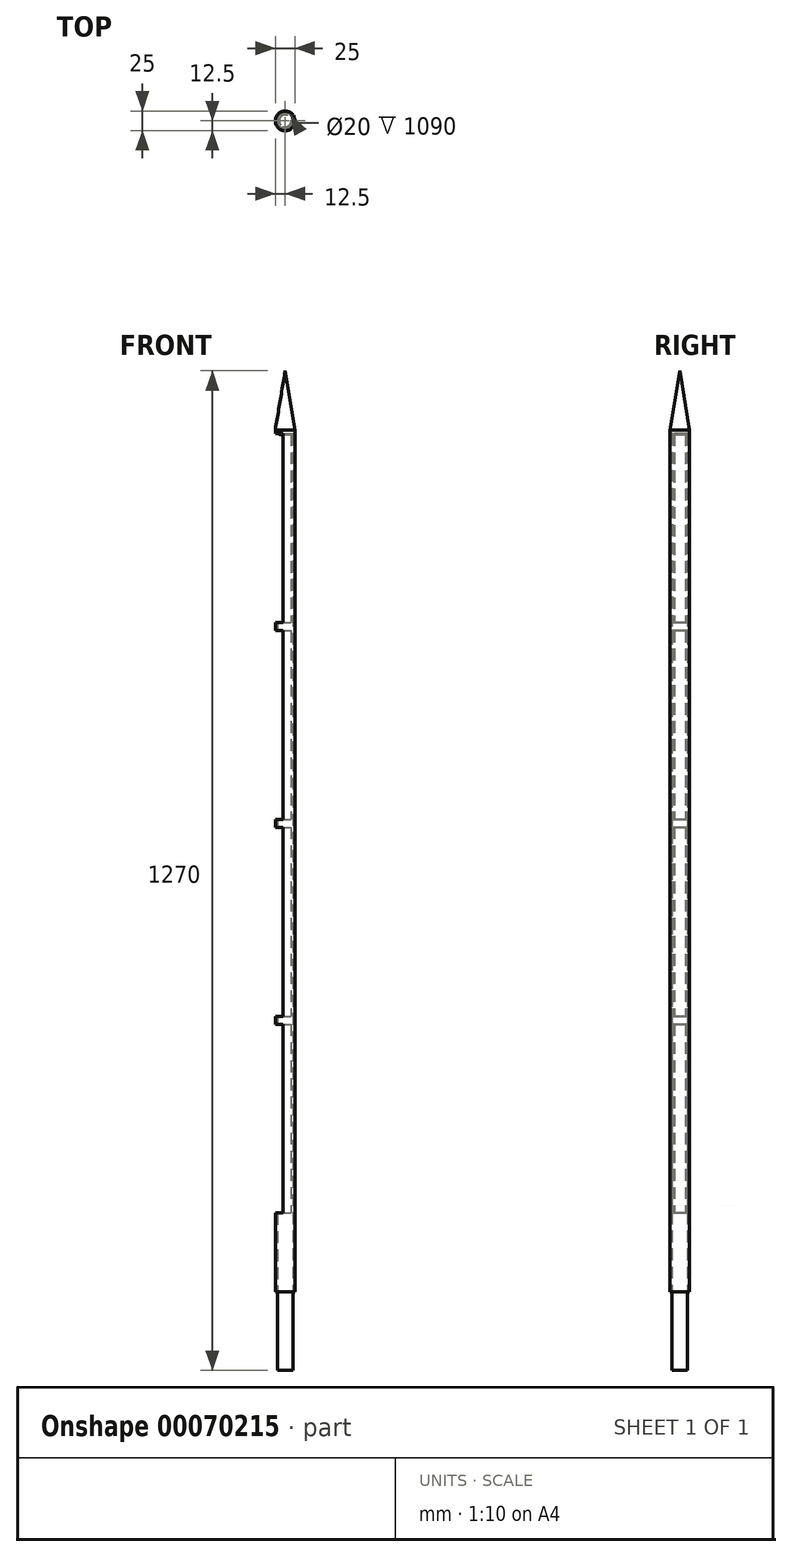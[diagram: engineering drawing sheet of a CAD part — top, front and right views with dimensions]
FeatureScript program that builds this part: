
annotation { "Feature Type Name" : "Feature", "Feature Type Description" : "" }
export const myFeature = defineFeature(function(context is Context, id is Id, definition is map)
    precondition{}
    {
        {
            var Q0;
            Q0=qCreatedBy(makeId("Top.planeOp"),FACE);
            var sketch = newSketch(context, id + "F0", { "sketchPlane" : qUnion([Q0])});
            skCircle(sketch, "E0", {"center": v(0, 0) * mm, "radius": 12.5 * mm});
            skCircle(sketch, "E1", {"center": v(0, 0) * mm, "radius": 9.9 * mm});
            skCircle(sketch, "E2", {"center": v(0, 0) * mm, "radius": 7.5 * mm});
            skCircle(sketch, "E3", {"center": v(0, 0) * mm, "radius": 10 * mm});
            skLineSegment(sketch, "E4", {"start": v(-18.54, 2.5) * mm, "end": v(18.35, 2.5) * mm, "construction": true});
            skSolve(sketch);
        }
        {
            var Q0;
            Q0=makeQuery(id+"F0.imprint","IMPRINT",FACE,{"disambiguationData":[TD([[makeQuery(id+"F0.imprint","IMPRINT",EDGE,{"derivedFrom":sQuery(id+"F0.wireOp",EDGE,"E0")}),1.0]])]});
            var Q1;
            Q1=makeQuery(id+"F0.imprint","IMPRINT",FACE,{"disambiguationData":[TD([[makeQuery(id+"F0.imprint","IMPRINT",EDGE,{"derivedFrom":sQuery(id+"F0.wireOp",EDGE,"E1")}),1.0]])]});
            extrude(context, id + "F1", {"entities" : qUnion([Q0, Q1]), "depth" : 1000 * mm});
        }
        {
            var Q0;
            Q0=qCreatedBy(makeId("Front.planeOp"),FACE);
            var sketch = newSketch(context, id + "F2", { "sketchPlane" : qUnion([Q0])});
            skLineSegment(sketch, "E5", {"start": v(12.5, 1000) * mm, "end": v(12.5, 0) * mm, "construction": true});
            skLineSegment(sketch, "E6", {"start": v(-12.5, 0) * mm, "end": v(-12.5, 1000) * mm, "construction": true});
            skLineSegment(sketch, "E7.bottom", {"start": v(-12.5, 10) * mm, "end": v(-2.5, 10) * mm});
            skLineSegment(sketch, "E7.top", {"start": v(-12.5, 250) * mm, "end": v(-2.5, 250) * mm});
            skLineSegment(sketch, "E7.left", {"start": v(-12.5, 10) * mm, "end": v(-12.5, 250) * mm});
            skLineSegment(sketch, "E7.right", {"start": v(-2.5, 10) * mm, "end": v(-2.5, 250) * mm});
            skLineSegment(sketch, "E8.0.1.0", {"start": v(-2.5, 260) * mm, "end": v(-2.5, 500) * mm});
            skLineSegment(sketch, "E8.0.1.1", {"start": v(-12.5, 500) * mm, "end": v(-2.5, 500) * mm});
            skLineSegment(sketch, "E8.0.1.2", {"start": v(-12.5, 260) * mm, "end": v(-12.5, 500) * mm});
            skLineSegment(sketch, "E8.0.1.3", {"start": v(-12.5, 260) * mm, "end": v(-2.5, 260) * mm});
            skLineSegment(sketch, "E8.0.2.0", {"start": v(-2.5, 510) * mm, "end": v(-2.5, 750) * mm});
            skLineSegment(sketch, "E8.0.2.1", {"start": v(-12.5, 750) * mm, "end": v(-2.5, 750) * mm});
            skLineSegment(sketch, "E8.0.2.2", {"start": v(-12.5, 510) * mm, "end": v(-12.5, 750) * mm});
            skLineSegment(sketch, "E8.0.2.3", {"start": v(-12.5, 510) * mm, "end": v(-2.5, 510) * mm});
            skLineSegment(sketch, "E8.0.3.0", {"start": v(-2.5, 760) * mm, "end": v(-2.5, 1000) * mm});
            skLineSegment(sketch, "E8.0.3.1", {"start": v(-12.5, 1000) * mm, "end": v(-2.5, 1000) * mm});
            skLineSegment(sketch, "E8.0.3.2", {"start": v(-12.5, 760) * mm, "end": v(-12.5, 1000) * mm});
            skLineSegment(sketch, "E8.0.3.3", {"start": v(-12.5, 760) * mm, "end": v(-2.5, 760) * mm});
            skLineSegment(sketch, "E8.direction1", {"start": v(-2.5, 10) * mm, "end": v(22.5, 10) * mm, "construction": true});
            skLineSegment(sketch, "E8.direction2", {"start": v(-2.5, 10) * mm, "end": v(-2.5, 260) * mm, "construction": true});
            skLineSegment(sketch, "E9.0", {"start": v(-9.9, 1000) * mm, "end": v(9.9, 1000) * mm, "construction": true});
            skSolve(sketch);
        }
        {
            var Q0;
            Q0 = qSketchRegion(id + "F2", true);
            extrude(context, id + "F3", {"entities" : qUnion([Q0]), "operationType" : NewBodyOperationType.REMOVE, "depth" : 25 * mm, "hasSecondDirection" : true, "secondDirectionOppositeDirection" : true, "secondDirectionDepth" : 25 * mm});
        }
        {
            var Q0;
            Q0=qCreatedBy(makeId("Front.planeOp"),FACE);
            var sketch = newSketch(context, id + "F4", { "sketchPlane" : qUnion([Q0])});
            skLineSegment(sketch, "E10", {"start": v(-9.9, 250) * mm, "end": v(-9.9, 260) * mm, "construction": true});
            skLineSegment(sketch, "E11", {"start": v(-9.9, 500) * mm, "end": v(-9.9, 510) * mm, "construction": true});
            skLineSegment(sketch, "E12", {"start": v(-9.9, 750) * mm, "end": v(-9.9, 760) * mm, "construction": true});
            skLineSegment(sketch, "E13", {"start": v(9.9, 1000) * mm, "end": v(9.9, 0) * mm, "construction": true});
            skLineSegment(sketch, "E14", {"start": v(-9.9, 0) * mm, "end": v(-9.9, 10) * mm, "construction": true});
            skLineSegment(sketch, "E15.bottom", {"start": v(-9.9, 250) * mm, "end": v(9.9, 250) * mm});
            skLineSegment(sketch, "E15.top", {"start": v(-9.9, 260) * mm, "end": v(9.9, 260) * mm});
            skLineSegment(sketch, "E15.left", {"start": v(-9.9, 250) * mm, "end": v(-9.9, 260) * mm});
            skLineSegment(sketch, "E15.right", {"start": v(9.9, 250) * mm, "end": v(9.9, 260) * mm});
            skLineSegment(sketch, "E16.bottom", {"start": v(-9.9, 500) * mm, "end": v(9.9, 500) * mm});
            skLineSegment(sketch, "E16.top", {"start": v(-9.9, 510) * mm, "end": v(9.9, 510) * mm});
            skLineSegment(sketch, "E16.left", {"start": v(-9.9, 500) * mm, "end": v(-9.9, 510) * mm});
            skLineSegment(sketch, "E16.right", {"start": v(9.9, 500) * mm, "end": v(9.9, 510) * mm});
            skLineSegment(sketch, "E17.bottom", {"start": v(-9.9, 750) * mm, "end": v(9.9, 750) * mm});
            skLineSegment(sketch, "E17.top", {"start": v(-9.9, 760) * mm, "end": v(9.9, 760) * mm});
            skLineSegment(sketch, "E17.left", {"start": v(-9.9, 750) * mm, "end": v(-9.9, 760) * mm});
            skLineSegment(sketch, "E17.right", {"start": v(9.9, 750) * mm, "end": v(9.9, 760) * mm});
            skLineSegment(sketch, "E18.bottom", {"start": v(-9.9, 0) * mm, "end": v(9.9, 0) * mm});
            skLineSegment(sketch, "E18.top", {"start": v(-9.9, 10) * mm, "end": v(9.9, 10) * mm});
            skLineSegment(sketch, "E18.left", {"start": v(-9.9, 0) * mm, "end": v(-9.9, 10) * mm});
            skLineSegment(sketch, "E18.right", {"start": v(9.9, 0) * mm, "end": v(9.9, 10) * mm});
            skLineSegment(sketch, "E19", {"start": v(-9.9, 1000) * mm, "end": v(9.9, 1000) * mm});
            skLineSegment(sketch, "E20", {"start": v(9.9, 1000) * mm, "end": v(9.9, 999.24) * mm});
            skLineSegment(sketch, "E21", {"start": v(9.9, 999.24) * mm, "end": v(-9.9, 999.24) * mm});
            skLineSegment(sketch, "E22", {"start": v(-9.9, 999.24) * mm, "end": v(-9.9, 1000) * mm});
            skSolve(sketch);
        }
        {
            var Q0;
            Q0 = qSketchRegion(id + "F4", true);
            var Q1;
            Q1=makeQuery(id+"F1.opExtrude","SWEPT_FACE",FACE,{"disambiguationData":[OSD([sQuery(id+"F0.wireOp",EDGE,"E2")])]});
            var Q2;
            Q2=makeQuery(id+"F1.opExtrude","SWEPT_BODY",BODY,{"disambiguationData":[OSD([sQuery(id+"F0.wireOp",EDGE,"E1"),sQuery(id+"F0.wireOp",EDGE,"E2")])]});
            var Q3;
            Q3=makeQuery(id+"F1.opExtrude","SWEPT_FACE",FACE,{"disambiguationData":[OSD([sQuery(id+"F0.wireOp",EDGE,"E2")])]});
            extrude(context, id + "F5", {"entities" : qUnion([Q0]), "operationType" : NewBodyOperationType.ADD, "endBound" : BoundingType.UP_TO_SURFACE, "endBoundEntityFace" : qUnion([Q1]), "endBoundEntityBody" : qUnion([Q2]), "depth" : 25 * mm});
        }
        {
            var Q0;
            Q0=makeQuery(id+"F1.opExtrude","SWEPT_BODY",BODY,{"disambiguationData":[OSD([sQuery(id+"F0.wireOp",EDGE,"E1"),sQuery(id+"F0.wireOp",EDGE,"E2")])]});
            var Q1;
            Q1=qCreatedBy(makeId("Front.planeOp"),FACE);
            mirror(context, id + "F6", {"operationType" : NewBodyOperationType.ADD, "entities" : qUnion([Q0]), "mirrorPlane" : qUnion([Q1])});
        }
        {
            var Q0;
            Q0=makeQuery(id+"F3Ne5Jxx6lpwAh3_2.boolean.opBoolean","MERGE",FACE,{"derivedFrom":[makeQuery(id+"F1.opExtrude","CAP_FACE",FACE,{"disambiguationData":[OSD([sQuery(id+"F0.wireOp",EDGE,"E0"),sQuery(id+"F0.wireOp",EDGE,"E3")])],"isStart":true}),makeQuery(id+"F3Ne5Jxx6lpwAh3_2.opExtrude","CAP_FACE",FACE,{"disambiguationData":[OSD([sQuery(id+"FG2CbKwcD7oa3Lb_2.wireOp",EDGE,"2d07a7d6-259c-4702-b32d-9226fc1d7e66"),sQuery(id+"FG2CbKwcD7oa3Lb_2.wireOp",EDGE,"FIqVUOIj-8J93-WVxq-X9l1-dofJ04PRRgEh"),sQuery(id+"FG2CbKwcD7oa3Lb_2.wireOp",EDGE,"LsVoywHY-rIsd-7w2n-b1Zv-yYyV3EzCeLPT"),sQuery(id+"FG2CbKwcD7oa3Lb_2.wireOp",EDGE,"kgGrGmKi-vCkJ-cQdU-GLAm-AZ3v8qjCPgoo"),sQuery(id+"FG2CbKwcD7oa3Lb_2.wireOp",EDGE,"rBjb7ZUO-rOm0-qUxf-SdPY-v9nMBaignq0d"),sQuery(id+"FG2CbKwcD7oa3Lb_2.wireOp",EDGE,"9e63ed98-5d8e-465b-b046-49ef0fd66d290.MirrorCS"),sQuery(id+"FG2CbKwcD7oa3Lb_2.wireOp",EDGE,"9e63ed98-5d8e-465b-b046-49ef0fd66d291.MirrorCS"),sQuery(id+"FG2CbKwcD7oa3Lb_2.wireOp",EDGE,"9e63ed98-5d8e-465b-b046-49ef0fd66d292.MirrorCS"),sQuery(id+"FG2CbKwcD7oa3Lb_2.wireOp",EDGE,"9e63ed98-5d8e-465b-b046-49ef0fd66d293.MirrorCS"),sQuery(id+"FG2CbKwcD7oa3Lb_2.wireOp",EDGE,"9e63ed98-5d8e-465b-b046-49ef0fd66d294.MirrorCS")])],"isStart":true})]});
            var sketch = newSketch(context, id + "F7", { "sketchPlane" : qUnion([Q0])});
            skCircle(sketch, "E23.0", {"center": v(0, 0) * mm, "radius": 9.9 * mm});
            skSolve(sketch);
        }
        {
            var Q0;
            Q0=makeQuery(id+"F1.opExtrude","CAP_FACE",FACE,{"disambiguationData":[OSD([sQuery(id+"F0.wireOp",EDGE,"E0"),sQuery(id+"F0.wireOp",EDGE,"E3")])],"isStart":false});
            var sketch = newSketch(context, id + "F8", { "sketchPlane" : qUnion([Q0])});
            skCircle(sketch, "E24", {"center": v(0, 0) * mm, "radius": 12.5 * mm});
            skSolve(sketch);
        }
        {
            var Q0;
            Q0 = qSketchRegion(id + "F8", true);
            extrude(context, id + "F9", {"entities" : qUnion([Q0]), "operationType" : NewBodyOperationType.ADD, "depth" : 5 * mm});
        }
        {
            var Q0;
            Q0 = qSketchRegion(id + "F7", true);
            extrude(context, id + "F10", {"entities" : qUnion([Q0]), "operationType" : NewBodyOperationType.ADD, "depth" : 190 * mm});
        }
        {
            var Q0;
            Q0=qCreatedBy(makeId("Front.planeOp"),FACE);
            var sketch = newSketch(context, id + "F11", { "sketchPlane" : qUnion([Q0])});
            skLineSegment(sketch, "E25", {"start": v(0, 1005) * mm, "end": v(12.5, 1005) * mm});
            skLineSegment(sketch, "E26", {"start": v(12.5, 1005) * mm, "end": v(0, 1080) * mm});
            skLineSegment(sketch, "E27", {"start": v(0, 1080) * mm, "end": v(0, 1005) * mm});
            skSolve(sketch);
        }
        {
            var Q0;
            Q0=makeQuery(id+"F11.imprint","IMPRINT",FACE,{"disambiguationData":[TD([[makeQuery(id+"F11.imprint","IMPRINT",EDGE,{"derivedFrom":sQuery(id+"F11.wireOp",EDGE,"E25")}),1.0]])]});
            var Q1;
            Q1=sQuery(id+"F11.wireOp",EDGE,"E27");
            revolve(context, id + "F12", {"operationType" : NewBodyOperationType.ADD, "entities" : qUnion([Q0]), "axis" : qUnion([Q1]), "revolveType" : RevolveType.FULL});
        }
        {
            var Q0;
            Q0=makeQuery(id+"F1.opExtrude","CAP_FACE",FACE,{"disambiguationData":[OSD([sQuery(id+"F0.wireOp",EDGE,"E0"),sQuery(id+"F0.wireOp",EDGE,"E3")])],"isStart":true});
            extrude(context, id + "F13", {"entities" : qUnion([Q0]), "operationType" : NewBodyOperationType.ADD, "depth" : 90 * mm});
        }
    });
